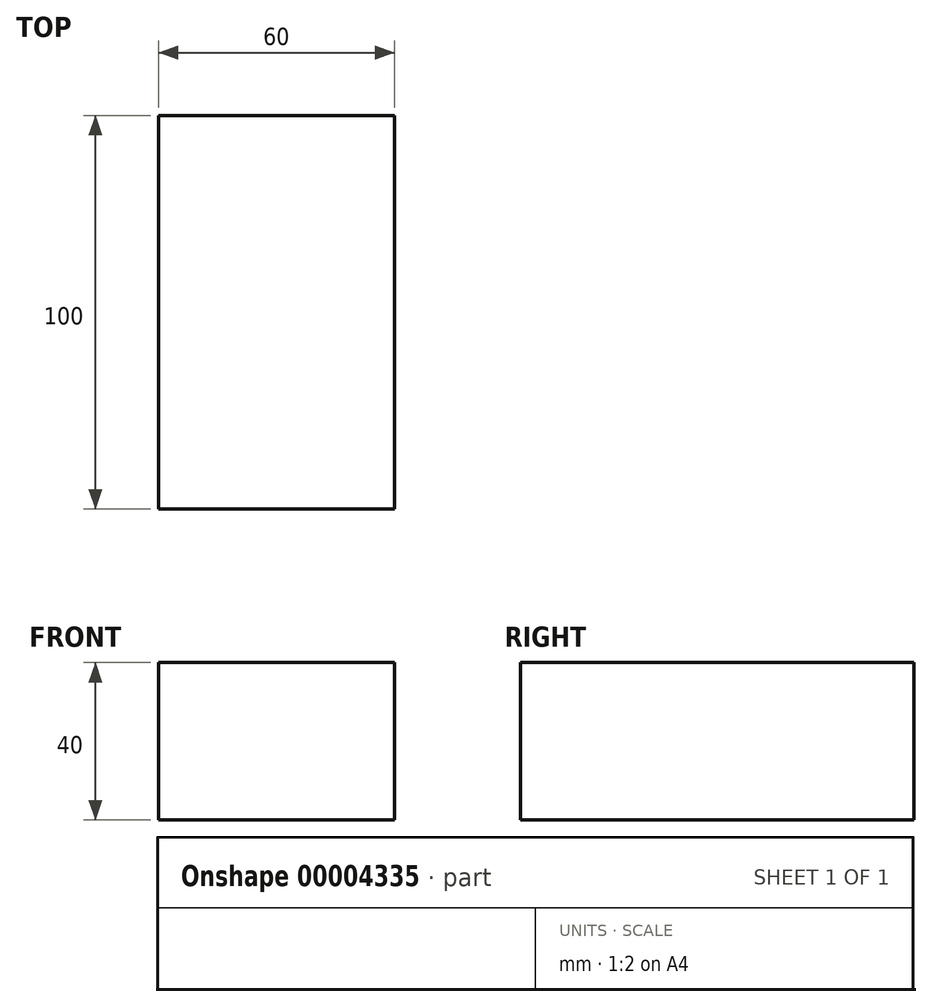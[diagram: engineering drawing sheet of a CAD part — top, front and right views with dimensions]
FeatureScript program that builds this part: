
annotation { "Feature Type Name" : "Feature", "Feature Type Description" : "" }
export const myFeature = defineFeature(function(context is Context, id is Id, definition is map)
    precondition{}
    {
        {
            var Q0;
            Q0=qCreatedBy(makeId("Front.planeOp"),FACE);
            var sketch = newSketch(context, id + "F0", { "sketchPlane" : qUnion([Q0])});
            skLineSegment(sketch, "E0", {"start": v(0, 0) * mm, "end": v(-30, 0) * mm});
            skLineSegment(sketch, "E1", {"start": v(0, 0) * mm, "end": v(30, 0) * mm});
            skLineSegment(sketch, "E2", {"start": v(-30, 0) * mm, "end": v(-30, 40) * mm});
            skLineSegment(sketch, "E3.0", {"start": v(30, 0) * mm, "end": v(30, 40) * mm});
            skLineSegment(sketch, "E4", {"start": v(-30, 40) * mm, "end": v(30, 40) * mm});
            skSolve(sketch);
        }
        {
            var Q0;
            Q0=makeQuery(id+"F0.imprint","IMPRINT",FACE,{"disambiguationData":[TD([[makeQuery(id+"F0.imprint","IMPRINT",EDGE,{"derivedFrom":sQuery(id+"F0.wireOp",EDGE,"E0")}),-1.0]])]});
            extrude(context, id + "F1", {"entities" : qUnion([Q0]), "depth" : 100 * mm});
        }
    });
